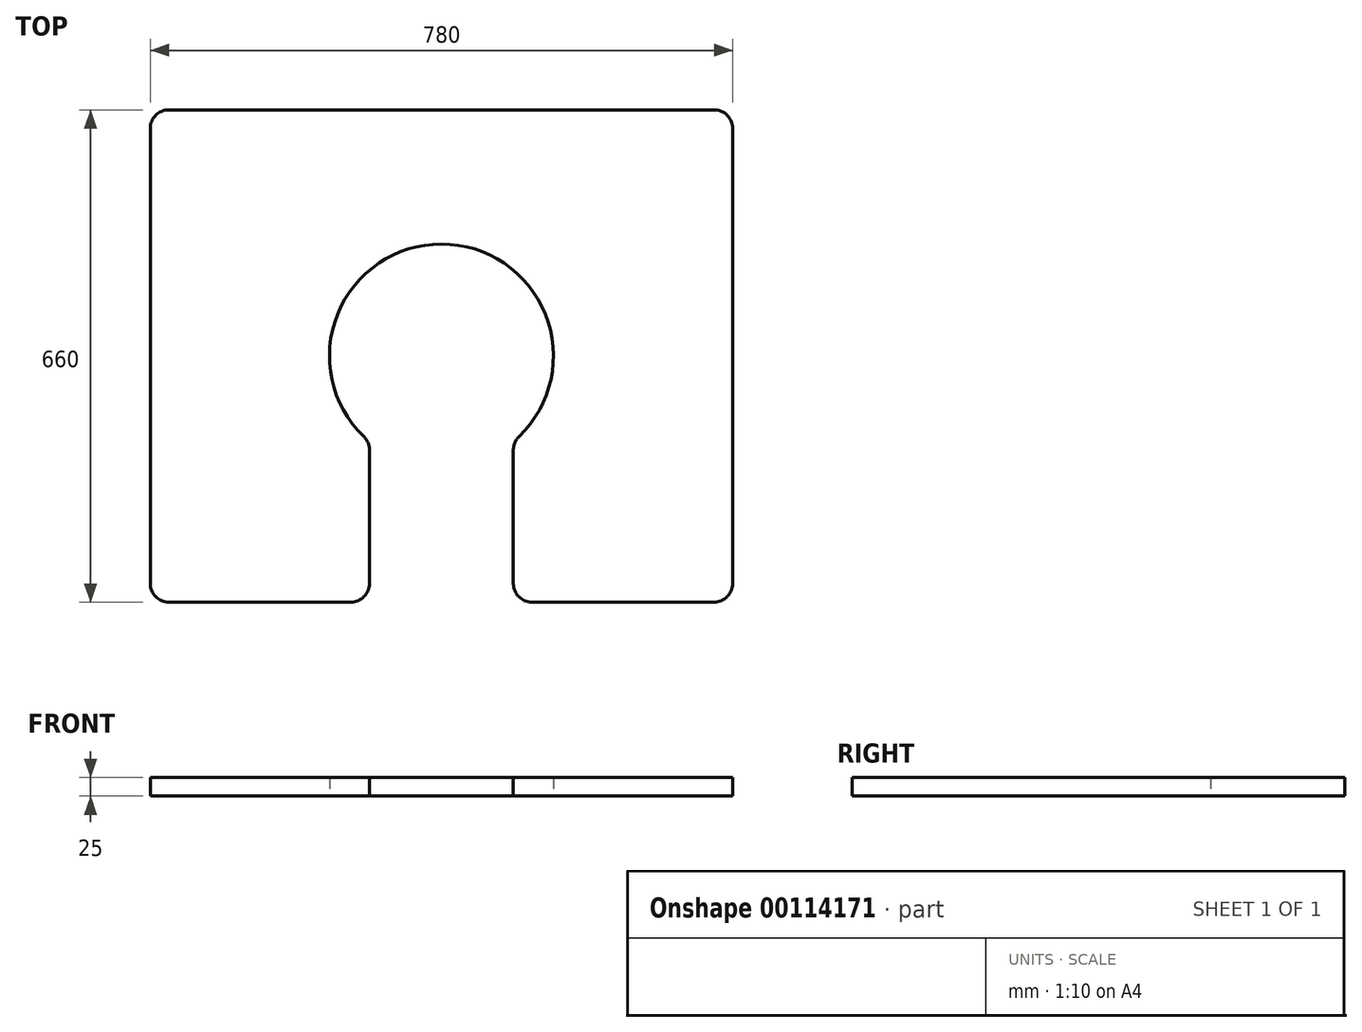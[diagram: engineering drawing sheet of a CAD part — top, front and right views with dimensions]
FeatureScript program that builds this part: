
annotation { "Feature Type Name" : "Feature", "Feature Type Description" : "" }
export const myFeature = defineFeature(function(context is Context, id is Id, definition is map)
    precondition{}
    {
        {
            var Q0;
            Q0=qCreatedBy(makeId("Top.planeOp"),FACE);
            var sketch = newSketch(context, id + "F0", { "sketchPlane" : qUnion([Q0])});
            skLineSegment(sketch, "E0.bottom", {"start": v(390, 330) * mm, "end": v(-390, 330) * mm});
            skLineSegment(sketch, "E0.top", {"start": v(390, -330) * mm, "end": v(-390, -330) * mm});
            skLineSegment(sketch, "E0.left", {"start": v(390, 330) * mm, "end": v(390, -330) * mm});
            skLineSegment(sketch, "E0.right", {"start": v(-390, 330) * mm, "end": v(-390, -330) * mm});
            skPoint(sketch, "E0.middle", {"position": v(0, 0) * mm});
            skCircle(sketch, "E1", {"center": v(0, 0) * mm, "radius": 150 * mm});
            skLineSegment(sketch, "E2", {"start": v(-96.35, -114.96) * mm, "end": v(-96.35, -330) * mm});
            skLineSegment(sketch, "E3", {"start": v(-96.35, -330) * mm, "end": v(0, -330) * mm});
            skLineSegment(sketch, "E4.MirrorCS", {"start": v(96.35, -114.96) * mm, "end": v(96.35, -330) * mm});
            skLineSegment(sketch, "E5.MirrorCS", {"start": v(96.35, -330) * mm, "end": v(0, -330) * mm});
            skSolve(sketch);
        }
        {
            var Q0;
            Q0=makeQuery(id+"F0.imprint","IMPRINT",FACE,{"disambiguationData":[TD([[makeQuery(id+"F0.imprint","IMPRINT",EDGE,{"derivedFrom":sQuery(id+"F0.wireOp",EDGE,"E0.bottom")}),1.0]])]});
            extrude(context, id + "F1", {"entities" : qUnion([Q0]), "depth" : 25 * mm});
        }
        {
            var Q0;
            Q0=makeQuery(id+"F1.opExtrude","SWEPT_EDGE",EDGE,{"disambiguationData":[OSD([sQuery(id+"F0.wireOp",EDGE,"E1"),sQuery(id+"F0.wireOp",EDGE,"E2")])]});
            var Q1;
            Q1=makeQuery(id+"F1.opExtrude","SWEPT_EDGE",EDGE,{"disambiguationData":[OSD([sQuery(id+"F0.wireOp",EDGE,"E1"),sQuery(id+"F0.wireOp",EDGE,"E4.MirrorCS")])]});
            var Q2;
            Q2=makeQuery(id+"F1.opExtrude","SWEPT_EDGE",EDGE,{"disambiguationData":[OSD([sQuery(id+"F0.wireOp",EDGE,"E0.top"),sQuery(id+"F0.wireOp",EDGE,"E4.MirrorCS"),sQuery(id+"F0.wireOp",EDGE,"E5.MirrorCS")])]});
            var Q3;
            Q3=makeQuery(id+"F1.opExtrude","SWEPT_EDGE",EDGE,{"disambiguationData":[OSD([sQuery(id+"F0.wireOp",EDGE,"E0.top"),sQuery(id+"F0.wireOp",EDGE,"E0.left")])]});
            var Q4;
            Q4=makeQuery(id+"F1.opExtrude","SWEPT_EDGE",EDGE,{"disambiguationData":[OSD([sQuery(id+"F0.wireOp",EDGE,"E0.top"),sQuery(id+"F0.wireOp",EDGE,"E2"),sQuery(id+"F0.wireOp",EDGE,"E3")])]});
            var Q5;
            Q5=makeQuery(id+"F1.opExtrude","SWEPT_EDGE",EDGE,{"disambiguationData":[OSD([sQuery(id+"F0.wireOp",EDGE,"E0.top"),sQuery(id+"F0.wireOp",EDGE,"E0.right")])]});
            var Q6;
            Q6=makeQuery(id+"F1.opExtrude","SWEPT_EDGE",EDGE,{"disambiguationData":[OSD([sQuery(id+"F0.wireOp",EDGE,"E0.bottom"),sQuery(id+"F0.wireOp",EDGE,"E0.left")])]});
            var Q7;
            Q7=makeQuery(id+"F1.opExtrude","SWEPT_EDGE",EDGE,{"disambiguationData":[OSD([sQuery(id+"F0.wireOp",EDGE,"E0.bottom"),sQuery(id+"F0.wireOp",EDGE,"E0.right")])]});
            fillet(context, id + "F2", {"entities" : qUnion([Q0, Q1, Q2, Q3, Q4, Q5, Q6, Q7]), "radius" : 25 * mm, "tangentPropagation" : true, "allowEdgeOverflow" : false});
        }
    });
